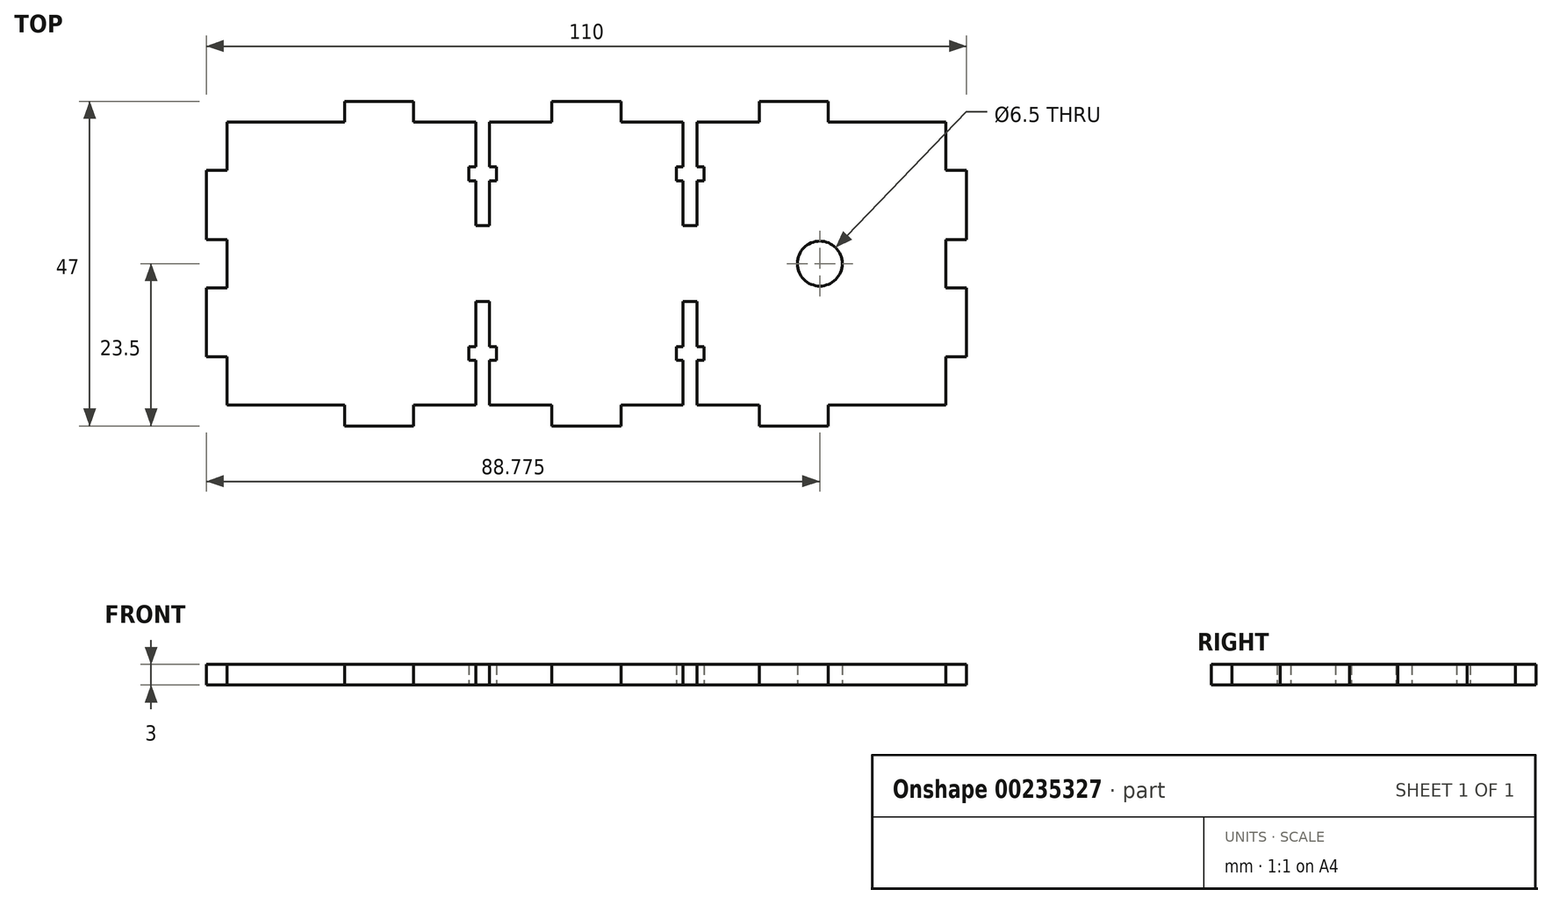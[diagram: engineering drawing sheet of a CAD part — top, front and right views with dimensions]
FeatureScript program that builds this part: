
annotation { "Feature Type Name" : "Feature", "Feature Type Description" : "" }
export const myFeature = defineFeature(function(context is Context, id is Id, definition is map)
    precondition{}
    {
        {
            var Q0;
            Q0=qCreatedBy(makeId("Top.planeOp"),FACE);
            var sketch = newSketch(context, id + "F0", { "sketchPlane" : qUnion([Q0])});
            skLineSegment(sketch, "E0", {"start": v(0, 0) * mm, "end": v(0, 7) * mm});
            skLineSegment(sketch, "E1", {"start": v(0, 7) * mm, "end": v(-3, 7) * mm});
            skLineSegment(sketch, "E2", {"start": v(-3, 7) * mm, "end": v(-3, 17) * mm});
            skLineSegment(sketch, "E3", {"start": v(-3, 17) * mm, "end": v(0, 17) * mm});
            skLineSegment(sketch, "E4", {"start": v(0, 17) * mm, "end": v(0, 24) * mm});
            skLineSegment(sketch, "E5", {"start": v(0, 24) * mm, "end": v(-3, 24) * mm});
            skLineSegment(sketch, "E6", {"start": v(-3, 24) * mm, "end": v(-3, 34) * mm});
            skLineSegment(sketch, "E7", {"start": v(-3, 34) * mm, "end": v(0, 34) * mm});
            skLineSegment(sketch, "E8", {"start": v(0, 34) * mm, "end": v(0, 41) * mm});
            skLineSegment(sketch, "E9", {"start": v(0, 41) * mm, "end": v(17, 41) * mm});
            skLineSegment(sketch, "E10", {"start": v(17, 41) * mm, "end": v(17, 44) * mm});
            skLineSegment(sketch, "E11", {"start": v(17, 44) * mm, "end": v(27, 44) * mm});
            skLineSegment(sketch, "E12", {"start": v(27, 44) * mm, "end": v(27, 41) * mm});
            skLineSegment(sketch, "E13", {"start": v(47, 41) * mm, "end": v(47, 44) * mm});
            skLineSegment(sketch, "E14", {"start": v(47, 44) * mm, "end": v(57, 44) * mm});
            skLineSegment(sketch, "E15", {"start": v(57, 44) * mm, "end": v(57, 41) * mm});
            skLineSegment(sketch, "E16", {"start": v(77, 41) * mm, "end": v(77, 44) * mm});
            skLineSegment(sketch, "E17", {"start": v(77, 44) * mm, "end": v(87, 44) * mm});
            skLineSegment(sketch, "E18", {"start": v(87, 44) * mm, "end": v(87, 41) * mm});
            skLineSegment(sketch, "E19", {"start": v(87, 41) * mm, "end": v(104, 41) * mm});
            skLineSegment(sketch, "E20", {"start": v(0, 20.5) * mm, "end": v(104, 20.5) * mm, "construction": true});
            skLineSegment(sketch, "E21.MirrorCS", {"start": v(-3, 7) * mm, "end": v(0, 7) * mm});
            skLineSegment(sketch, "E22.MirrorCS", {"start": v(0, 7) * mm, "end": v(0, 0) * mm});
            skLineSegment(sketch, "E23.MirrorCS", {"start": v(0, 0) * mm, "end": v(17, 0) * mm});
            skLineSegment(sketch, "E24.MirrorCS", {"start": v(17, 0) * mm, "end": v(17, -3) * mm});
            skLineSegment(sketch, "E25.MirrorCS", {"start": v(27, -3) * mm, "end": v(27, 0) * mm});
            skLineSegment(sketch, "E26.MirrorCS", {"start": v(87, -3) * mm, "end": v(87, 0) * mm});
            skLineSegment(sketch, "E27.MirrorCS", {"start": v(77, -3) * mm, "end": v(87, -3) * mm});
            skLineSegment(sketch, "E28.MirrorCS", {"start": v(77, 0) * mm, "end": v(77, -3) * mm});
            skLineSegment(sketch, "E29.MirrorCS", {"start": v(87, 0) * mm, "end": v(104, 0) * mm});
            skLineSegment(sketch, "E30.MirrorCS", {"start": v(17, -3) * mm, "end": v(27, -3) * mm});
            skLineSegment(sketch, "E31.MirrorCS", {"start": v(47, 0) * mm, "end": v(47, -3) * mm});
            skLineSegment(sketch, "E32.MirrorCS", {"start": v(47, -3) * mm, "end": v(57, -3) * mm});
            skLineSegment(sketch, "E33.MirrorCS", {"start": v(57, -3) * mm, "end": v(57, 0) * mm});
            skLineSegment(sketch, "E34", {"start": v(52, 44) * mm, "end": v(52, -3) * mm, "construction": true});
            skLineSegment(sketch, "E35.MirrorCS", {"start": v(104, 7) * mm, "end": v(107, 7) * mm});
            skLineSegment(sketch, "E36.MirrorCS", {"start": v(107, 7) * mm, "end": v(104, 7) * mm});
            skLineSegment(sketch, "E37.MirrorCS", {"start": v(107, 34) * mm, "end": v(104, 34) * mm});
            skLineSegment(sketch, "E38.MirrorCS", {"start": v(104, 24) * mm, "end": v(107, 24) * mm});
            skLineSegment(sketch, "E39.MirrorCS", {"start": v(107, 17) * mm, "end": v(104, 17) * mm});
            skLineSegment(sketch, "E40.MirrorCS", {"start": v(104, 7) * mm, "end": v(104, 0) * mm});
            skLineSegment(sketch, "E41.MirrorCS", {"start": v(104, 17) * mm, "end": v(104, 24) * mm});
            skLineSegment(sketch, "E42.MirrorCS", {"start": v(104, 0) * mm, "end": v(104, 7) * mm});
            skLineSegment(sketch, "E43.MirrorCS", {"start": v(104, 34) * mm, "end": v(104, 41) * mm});
            skLineSegment(sketch, "E44.MirrorCS", {"start": v(107, 7) * mm, "end": v(107, 17) * mm});
            skLineSegment(sketch, "E45.MirrorCS", {"start": v(107, 24) * mm, "end": v(107, 34) * mm});
            skLineSegment(sketch, "E46", {"start": v(27, 41) * mm, "end": v(36, 41) * mm});
            skLineSegment(sketch, "E47", {"start": v(47, 41) * mm, "end": v(38, 41) * mm});
            skLineSegment(sketch, "E48", {"start": v(36, 41) * mm, "end": v(36, 34.5) * mm});
            skLineSegment(sketch, "E49", {"start": v(38, 41) * mm, "end": v(38, 34.5) * mm});
            skLineSegment(sketch, "E50", {"start": v(36, 34.5) * mm, "end": v(35, 34.5) * mm});
            skLineSegment(sketch, "E51", {"start": v(35, 34.5) * mm, "end": v(35, 32.5) * mm});
            skLineSegment(sketch, "E52", {"start": v(35, 32.5) * mm, "end": v(36, 32.5) * mm});
            skLineSegment(sketch, "E53", {"start": v(38, 34.5) * mm, "end": v(39, 34.5) * mm});
            skLineSegment(sketch, "E54", {"start": v(39, 34.5) * mm, "end": v(39, 32.5) * mm});
            skLineSegment(sketch, "E55", {"start": v(36, 32.5) * mm, "end": v(36, 26) * mm});
            skLineSegment(sketch, "E56", {"start": v(39, 32.5) * mm, "end": v(38, 32.5) * mm});
            skLineSegment(sketch, "E57", {"start": v(38, 32.5) * mm, "end": v(38, 26) * mm});
            skLineSegment(sketch, "E58", {"start": v(38, 26) * mm, "end": v(36, 26) * mm});
            skLineSegment(sketch, "E59.MirrorCS", {"start": v(69, 34.5) * mm, "end": v(69, 32.5) * mm});
            skLineSegment(sketch, "E60.MirrorCS", {"start": v(65, 34.5) * mm, "end": v(65, 32.5) * mm});
            skLineSegment(sketch, "E61.MirrorCS", {"start": v(66, 34.5) * mm, "end": v(65, 34.5) * mm});
            skLineSegment(sketch, "E62.MirrorCS", {"start": v(68, 34.5) * mm, "end": v(69, 34.5) * mm});
            skLineSegment(sketch, "E63.MirrorCS", {"start": v(65, 32.5) * mm, "end": v(66, 32.5) * mm});
            skLineSegment(sketch, "E64.MirrorCS", {"start": v(69, 32.5) * mm, "end": v(68, 32.5) * mm});
            skLineSegment(sketch, "E65.MirrorCS", {"start": v(66, 26) * mm, "end": v(68, 26) * mm});
            skLineSegment(sketch, "E66.MirrorCS", {"start": v(66, 41) * mm, "end": v(66, 34.5) * mm});
            skLineSegment(sketch, "E67.MirrorCS", {"start": v(66, 32.5) * mm, "end": v(66, 26) * mm});
            skLineSegment(sketch, "E68.MirrorCS", {"start": v(68, 41) * mm, "end": v(68, 34.5) * mm});
            skLineSegment(sketch, "E69.MirrorCS", {"start": v(68, 32.5) * mm, "end": v(68, 26) * mm});
            skLineSegment(sketch, "E70.MirrorCS", {"start": v(104, 20.5) * mm, "end": v(0, 20.5) * mm, "construction": true});
            skLineSegment(sketch, "E71.MirrorCS", {"start": v(35, 8.5) * mm, "end": v(36, 8.5) * mm});
            skLineSegment(sketch, "E72.MirrorCS", {"start": v(39, 8.5) * mm, "end": v(38, 8.5) * mm});
            skLineSegment(sketch, "E73.MirrorCS", {"start": v(35, 6.5) * mm, "end": v(35, 8.5) * mm});
            skLineSegment(sketch, "E74.MirrorCS", {"start": v(36, 6.5) * mm, "end": v(35, 6.5) * mm});
            skLineSegment(sketch, "E75.MirrorCS", {"start": v(39, 6.5) * mm, "end": v(39, 8.5) * mm});
            skLineSegment(sketch, "E76.MirrorCS", {"start": v(38, 6.5) * mm, "end": v(39, 6.5) * mm});
            skLineSegment(sketch, "E77.MirrorCS", {"start": v(38, 15) * mm, "end": v(36, 15) * mm});
            skLineSegment(sketch, "E78.MirrorCS", {"start": v(38, 8.5) * mm, "end": v(38, 15) * mm});
            skLineSegment(sketch, "E79.MirrorCS", {"start": v(38, 0) * mm, "end": v(38, 6.5) * mm});
            skLineSegment(sketch, "E80.MirrorCS", {"start": v(36, 0) * mm, "end": v(36, 6.5) * mm});
            skLineSegment(sketch, "E81.MirrorCS", {"start": v(36, 8.5) * mm, "end": v(36, 15) * mm});
            skLineSegment(sketch, "E82.MirrorCS", {"start": v(69, 8.5) * mm, "end": v(68, 8.5) * mm});
            skLineSegment(sketch, "E83.MirrorCS", {"start": v(69, 6.5) * mm, "end": v(69, 8.5) * mm});
            skLineSegment(sketch, "E84.MirrorCS", {"start": v(65, 6.5) * mm, "end": v(65, 8.5) * mm});
            skLineSegment(sketch, "E85.MirrorCS", {"start": v(68, 6.5) * mm, "end": v(69, 6.5) * mm});
            skLineSegment(sketch, "E86.MirrorCS", {"start": v(65, 8.5) * mm, "end": v(66, 8.5) * mm});
            skLineSegment(sketch, "E87.MirrorCS", {"start": v(66, 15) * mm, "end": v(68, 15) * mm});
            skLineSegment(sketch, "E88.MirrorCS", {"start": v(66, 6.5) * mm, "end": v(65, 6.5) * mm});
            skLineSegment(sketch, "E89.MirrorCS", {"start": v(68, 0) * mm, "end": v(68, 6.5) * mm});
            skLineSegment(sketch, "E90.MirrorCS", {"start": v(66, 0) * mm, "end": v(66, 6.5) * mm});
            skLineSegment(sketch, "E91.MirrorCS", {"start": v(66, 8.5) * mm, "end": v(66, 15) * mm});
            skLineSegment(sketch, "E92.MirrorCS", {"start": v(68, 8.5) * mm, "end": v(68, 15) * mm});
            skLineSegment(sketch, "E93.MirrorCS", {"start": v(27, 0) * mm, "end": v(36, 0) * mm});
            skLineSegment(sketch, "E94.MirrorCS", {"start": v(52, -3) * mm, "end": v(52, 44) * mm, "construction": true});
            skLineSegment(sketch, "E95.MirrorCS", {"start": v(47, 0) * mm, "end": v(38, 0) * mm});
            skLineSegment(sketch, "E96", {"start": v(57, 41) * mm, "end": v(66, 41) * mm});
            skLineSegment(sketch, "E97", {"start": v(68, 41) * mm, "end": v(77, 41) * mm});
            skLineSegment(sketch, "E98", {"start": v(57, 0) * mm, "end": v(66, 0) * mm});
            skLineSegment(sketch, "E99", {"start": v(77, 0) * mm, "end": v(68, 0) * mm});
            skCircle(sketch, "E100", {"center": v(85.78, 20.5) * mm, "radius": 3.25 * mm});
            skSolve(sketch);
        }
        {
            var Q0;
            Q0=makeQuery(id+"F0.imprint","IMPRINT",FACE,{"disambiguationData":[TD([[makeQuery(id+"F0.imprint","IMPRINT",EDGE,{"derivedFrom":sQuery(id+"F0.wireOp",EDGE,"E61.MirrorCS")}),1.0]])]});
            var Q1;
            Q1=makeQuery(id+"F0.imprint","IMPRINT",FACE,{"disambiguationData":[TD([[makeQuery(id+"F0.imprint","IMPRINT",EDGE,{"derivedFrom":sQuery(id+"F0.wireOp",EDGE,"E221.MirrorCS")}),1.0]])]});
            var Q2;
            Q2=makeQuery(id+"F0.imprint","IMPRINT",FACE,{"disambiguationData":[TD([[makeQuery(id+"F0.imprint","IMPRINT",EDGE,{"derivedFrom":sQuery(id+"F0.wireOp",EDGE,"E82.MirrorCS")}),1.0]])]});
            var Q3;
            Q3=makeQuery(id+"F0.imprint","IMPRINT",FACE,{"disambiguationData":[TD([[makeQuery(id+"F0.imprint","IMPRINT",EDGE,{"derivedFrom":sQuery(id+"F0.wireOp",EDGE,"E2")}),-1.0]])]});
            extrude(context, id + "F1", {"entities" : qUnion([Q0, Q1, Q2, Q3]), "depth" : 3 * mm});
        }
    });
